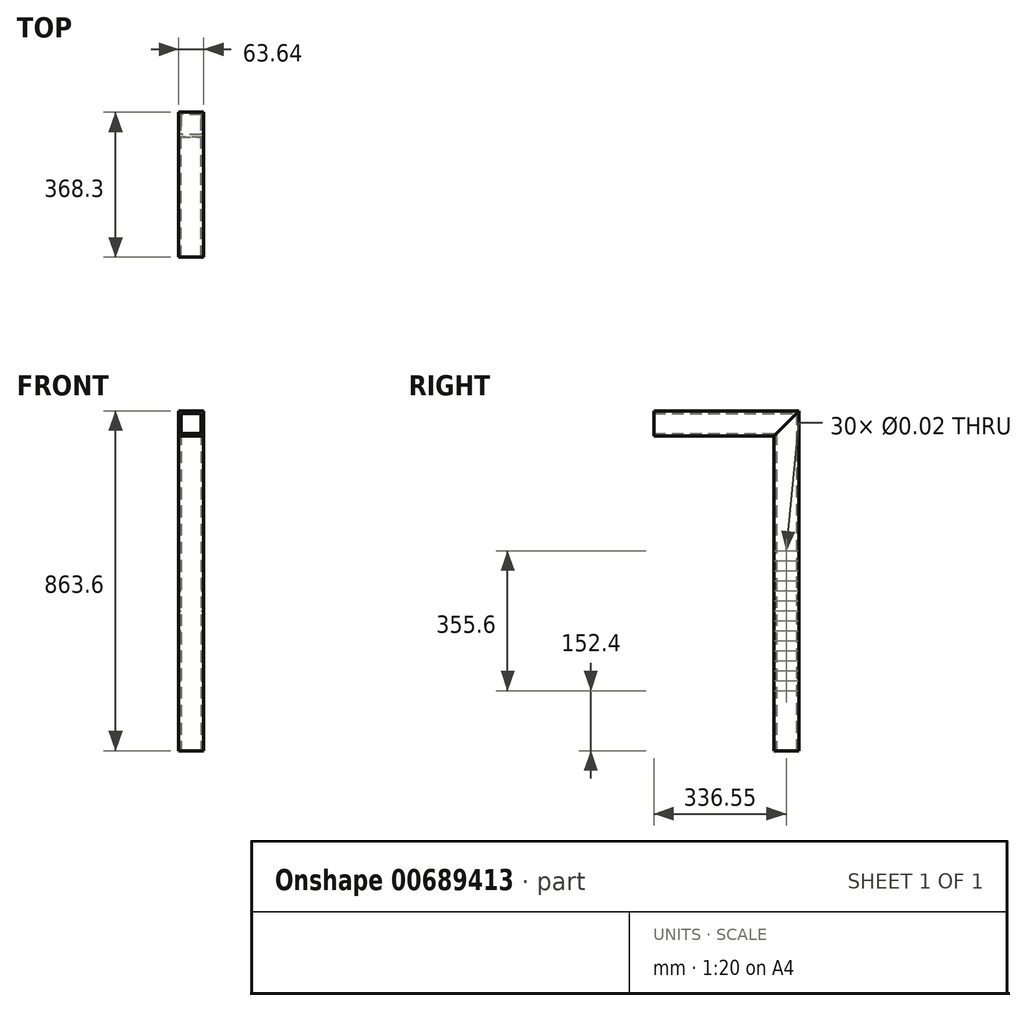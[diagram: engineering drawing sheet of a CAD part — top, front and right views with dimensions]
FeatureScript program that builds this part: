
annotation { "Feature Type Name" : "Feature", "Feature Type Description" : "" }
export const myFeature = defineFeature(function(context is Context, id is Id, definition is map)
    precondition{}
    {
        {
            var Q0;
            Q0=qCreatedBy(makeId("Top.planeOp"),FACE);
            var sketch = newSketch(context, id + "F0", { "sketchPlane" : qUnion([Q0])});
            skLineSegment(sketch, "E0.bottom", {"start": v(-31.75, 31.75) * mm, "end": v(31.75, 31.75) * mm});
            skLineSegment(sketch, "E0.top", {"start": v(-31.75, -31.75) * mm, "end": v(31.75, -31.75) * mm});
            skLineSegment(sketch, "E0.left", {"start": v(-31.75, 31.75) * mm, "end": v(-31.75, -31.75) * mm});
            skLineSegment(sketch, "E0.right", {"start": v(31.75, 31.75) * mm, "end": v(31.75, -31.75) * mm});
            skPoint(sketch, "E0.middle", {"position": v(0, 0) * mm});
            skLineSegment(sketch, "E1.bottom", {"start": v(-25.4, 25.4) * mm, "end": v(25.4, 25.4) * mm});
            skLineSegment(sketch, "E1.top", {"start": v(-25.4, -25.4) * mm, "end": v(25.4, -25.4) * mm});
            skLineSegment(sketch, "E1.left", {"start": v(-25.4, 25.4) * mm, "end": v(-25.4, -25.4) * mm});
            skLineSegment(sketch, "E1.right", {"start": v(25.4, 25.4) * mm, "end": v(25.4, -25.4) * mm});
            skSolve(sketch);
        }
        {
            var Q0;
            Q0=makeQuery(id+"F0.imprint","IMPRINT",FACE,{"disambiguationData":[TD([[makeQuery(id+"F0.imprint","IMPRINT",EDGE,{"derivedFrom":sQuery(id+"F0.wireOp",EDGE,"E0.bottom")}),-1.0]])]});
            extrude(context, id + "F1", {"entities" : qUnion([Q0]), "depth" : 863.6 * mm, "offsetDistance" : 25.4 * mm});
        }
        {
            var Q0;
            Q0=makeQuery(id+"F1.opExtrude","SWEPT_FACE",FACE,{"disambiguationData":[OSD([sQuery(id+"F0.wireOp",EDGE,"E0.right")])]});
            var sketch = newSketch(context, id + "F2", { "sketchPlane" : qUnion([Q0])});
            skLineSegment(sketch, "E2", {"start": v(31.75, 863.6) * mm, "end": v(-31.75, 863.6) * mm});
            skLineSegment(sketch, "E3", {"start": v(-31.75, 863.6) * mm, "end": v(-31.75, 800.1) * mm});
            skLineSegment(sketch, "E4", {"start": v(-31.75, 800.1) * mm, "end": v(31.75, 863.6) * mm});
            skSolve(sketch);
        }
        {
            var Q0;
            Q0=makeQuery(id+"F2.imprint","IMPRINT",FACE,{"disambiguationData":[TD([[makeQuery(id+"F2.imprint","IMPRINT",EDGE,{"derivedFrom":sQuery(id+"F2.wireOp",EDGE,"E2")}),1.0]])]});
            extrude(context, id + "F3", {"entities" : qUnion([Q0]), "operationType" : NewBodyOperationType.REMOVE, "oppositeDirection" : true, "depth" : 63.5 * mm, "offsetDistance" : 25.4 * mm});
        }
        {
            var Q0;
            Q0=makeQuery(id+"F1.opExtrude","SWEPT_FACE",FACE,{"disambiguationData":[OSD([sQuery(id+"F0.wireOp",EDGE,"E0.right")])]});
            var sketch = newSketch(context, id + "F4", { "sketchPlane" : qUnion([Q0])});
            skPoint(sketch, "E5", {"position": v(0, 152.4) * mm});
            skPoint(sketch, "E6.0.1.0", {"position": v(0, 177.8) * mm});
            skPoint(sketch, "E6.0.2.0", {"position": v(0, 203.2) * mm});
            skPoint(sketch, "E6.0.3.0", {"position": v(0, 228.6) * mm});
            skPoint(sketch, "E6.0.4.0", {"position": v(0, 254) * mm});
            skPoint(sketch, "E6.0.5.0", {"position": v(0, 279.4) * mm});
            skPoint(sketch, "E6.0.6.0", {"position": v(0, 304.8) * mm});
            skPoint(sketch, "E6.0.7.0", {"position": v(0, 330.2) * mm});
            skPoint(sketch, "E6.0.8.0", {"position": v(0, 355.6) * mm});
            skPoint(sketch, "E6.0.9.0", {"position": v(0, 381) * mm});
            skPoint(sketch, "E6.0.10.0", {"position": v(0, 406.4) * mm});
            skPoint(sketch, "E6.0.11.0", {"position": v(0, 431.8) * mm});
            skPoint(sketch, "E6.0.12.0", {"position": v(0, 457.2) * mm});
            skPoint(sketch, "E6.0.13.0", {"position": v(0, 482.6) * mm});
            skPoint(sketch, "E6.0.14.0", {"position": v(0, 508) * mm});
            skLineSegment(sketch, "E6.direction1", {"start": v(0, 152.4) * mm, "end": v(25.4, 152.4) * mm, "construction": true});
            skLineSegment(sketch, "E6.direction2", {"start": v(0, 152.4) * mm, "end": v(0, 177.8) * mm, "construction": true});
            skSolve(sketch);
        }
        {
            var Q0;
            Q0=sQuery(id+"F4.wireOp",VERTEX,"E5");
            var Q1;
            Q1=sQuery(id+"F4.wireOp",VERTEX,"E6.0.1.0");
            var Q2;
            Q2=sQuery(id+"F4.wireOp",VERTEX,"E6.0.2.0");
            var Q3;
            Q3=sQuery(id+"F4.wireOp",VERTEX,"E6.0.3.0");
            var Q4;
            Q4=sQuery(id+"F4.wireOp",VERTEX,"E6.0.4.0");
            var Q5;
            Q5=sQuery(id+"F4.wireOp",VERTEX,"E6.0.5.0");
            var Q6;
            Q6=sQuery(id+"F4.wireOp",VERTEX,"E6.0.6.0");
            var Q7;
            Q7=sQuery(id+"F4.wireOp",VERTEX,"E6.0.7.0");
            var Q8;
            Q8=sQuery(id+"F4.wireOp",VERTEX,"E6.0.8.0");
            var Q9;
            Q9=sQuery(id+"F4.wireOp",VERTEX,"E6.0.9.0");
            var Q10;
            Q10=sQuery(id+"F4.wireOp",VERTEX,"E6.0.11.0");
            var Q11;
            Q11=sQuery(id+"F4.wireOp",VERTEX,"E6.0.10.0");
            var Q12;
            Q12=sQuery(id+"F4.wireOp",VERTEX,"E6.0.12.0");
            var Q13;
            Q13=sQuery(id+"F4.wireOp",VERTEX,"E6.0.13.0");
            var Q14;
            Q14=sQuery(id+"F4.wireOp",VERTEX,"E6.0.14.0");
            var Q15;
            Q15=makeQuery(id+"F1.opExtrude","SWEPT_BODY",BODY,{"disambiguationData":[OSD([sQuery(id+"F0.wireOp",EDGE,"E0.bottom"),sQuery(id+"F0.wireOp",EDGE,"E0.top"),sQuery(id+"F0.wireOp",EDGE,"E0.left"),sQuery(id+"F0.wireOp",EDGE,"E0.right"),sQuery(id+"F0.wireOp",EDGE,"E1.bottom"),sQuery(id+"F0.wireOp",EDGE,"E1.top"),sQuery(id+"F0.wireOp",EDGE,"E1.left"),sQuery(id+"F0.wireOp",EDGE,"E1.right")])]});
            hole(context, id + "F5", {"style" : HoleStyle.SIMPLE, "endStyle" : HoleEndStyle.THROUGH, "standardTappedOrClearance" : lookupTablePath({ "standard" : "ANSI", "size" : "1/2 (0.5)", "type" : "Drilled" }), "standardBlindInLast" : lookupTablePath({ "standard" : "ANSI", "size" : "1/2", "type" : "Drilled" }), "holeDiameter" : 1 / 50.8 * mm, "majorDiameter" : 6.35 * mm, "tappedDepth" : 10.3 * mm, "tapClearance" : 3, "locations" : qUnion([Q0, Q1, Q2, Q3, Q4, Q5, Q6, Q7, Q8, Q9, Q10, Q11, Q12, Q13, Q14]), "scope" : qUnion([Q15])});
        }
        {
            var Q0;
            Q0=qCreatedBy(makeId("Front.planeOp"),FACE);
            var sketch = newSketch(context, id + "F6", { "sketchPlane" : qUnion([Q0])});
            skLineSegment(sketch, "E7.bottom", {"start": v(31.6, 0) * mm, "end": v(-31.9, 0) * mm});
            skLineSegment(sketch, "E7.top", {"start": v(31.6, -63.5) * mm, "end": v(-31.9, -63.5) * mm});
            skLineSegment(sketch, "E7.left", {"start": v(31.6, 0) * mm, "end": v(31.6, -63.5) * mm});
            skLineSegment(sketch, "E7.right", {"start": v(-31.9, 0) * mm, "end": v(-31.9, -63.5) * mm});
            skLineSegment(sketch, "E8.bottom", {"start": v(25.4, -6.35) * mm, "end": v(-25.4, -6.35) * mm});
            skLineSegment(sketch, "E8.top", {"start": v(25.4, -57.15) * mm, "end": v(-25.4, -57.15) * mm});
            skLineSegment(sketch, "E8.left", {"start": v(25.4, -6.35) * mm, "end": v(25.4, -57.15) * mm});
            skLineSegment(sketch, "E8.right", {"start": v(-25.4, -6.35) * mm, "end": v(-25.4, -57.15) * mm});
            skPoint(sketch, "E8.middle", {"position": v(0, -31.75) * mm});
            skSolve(sketch);
        }
        {
            var Q0;
            Q0=makeQuery(id+"F6.imprint","IMPRINT",FACE,{"disambiguationData":[TD([[makeQuery(id+"F6.imprint","IMPRINT",EDGE,{"derivedFrom":sQuery(id+"F6.wireOp",EDGE,"E7.bottom")}),1.0]])]});
            extrude(context, id + "F7", {"entities" : qUnion([Q0]), "depth" : 368.3 * mm, "offsetDistance" : 25.4 * mm});
        }
        {
            var Q0;
            Q0=makeQuery(id+"F7.opExtrude","SWEPT_BODY",BODY,{"disambiguationData":[OSD([sQuery(id+"F6.wireOp",EDGE,"E7.bottom"),sQuery(id+"F6.wireOp",EDGE,"E7.top"),sQuery(id+"F6.wireOp",EDGE,"E7.left"),sQuery(id+"F6.wireOp",EDGE,"E7.right"),sQuery(id+"F6.wireOp",EDGE,"E8.bottom"),sQuery(id+"F6.wireOp",EDGE,"E8.top"),sQuery(id+"F6.wireOp",EDGE,"E8.left"),sQuery(id+"F6.wireOp",EDGE,"E8.right")])]});
            var Q1;
            Q1=qCreatedBy(makeId("Front.planeOp"),FACE);
            transform(context, id + "F8", {"entities" : qUnion([Q0]), "transformType" : TransformType.TRANSLATION_DISTANCE, "transformDirection" : qUnion([Q1]), "distance" : 31.75 * mm, "oppositeDirection" : true, "makeCopy" : false});
        }
        {
            var Q0;
            Q0=makeQuery(id+"F7.opExtrude","SWEPT_FACE",FACE,{"disambiguationData":[OSD([sQuery(id+"F6.wireOp",EDGE,"E7.right")])]});
            var sketch = newSketch(context, id + "F9", { "sketchPlane" : qUnion([Q0])});
            skLineSegment(sketch, "E9", {"start": v(-31.75, 0) * mm, "end": v(-31.75, -63.5) * mm});
            skLineSegment(sketch, "E10", {"start": v(-31.75, -63.5) * mm, "end": v(31.75, -63.5) * mm});
            skLineSegment(sketch, "E11", {"start": v(31.75, -63.5) * mm, "end": v(-31.75, 0) * mm});
            skSolve(sketch);
        }
        {
            var Q0;
            Q0=makeQuery(id+"F9.imprint","IMPRINT",FACE,{"disambiguationData":[TD([[makeQuery(id+"F9.imprint","IMPRINT",EDGE,{"derivedFrom":sQuery(id+"F9.wireOp",EDGE,"E9")}),1.0]])]});
            extrude(context, id + "F10", {"entities" : qUnion([Q0]), "operationType" : NewBodyOperationType.REMOVE, "oppositeDirection" : true, "depth" : 63.5 * mm, "offsetDistance" : 25.4 * mm});
        }
        {
            var Q0;
            Q0=makeQuery(id+"F7.opExtrude","SWEPT_BODY",BODY,{"disambiguationData":[OSD([sQuery(id+"F6.wireOp",EDGE,"E7.bottom"),sQuery(id+"F6.wireOp",EDGE,"E7.top"),sQuery(id+"F6.wireOp",EDGE,"E7.left"),sQuery(id+"F6.wireOp",EDGE,"E7.right"),sQuery(id+"F6.wireOp",EDGE,"E8.bottom"),sQuery(id+"F6.wireOp",EDGE,"E8.top"),sQuery(id+"F6.wireOp",EDGE,"E8.left"),sQuery(id+"F6.wireOp",EDGE,"E8.right")])]});
            var Q1;
            Q1=qCreatedBy(makeId("Top.planeOp"),FACE);
            transform(context, id + "F11", {"entities" : qUnion([Q0]), "transformType" : TransformType.TRANSLATION_DISTANCE, "transformDirection" : qUnion([Q1]), "distance" : 863.6 * mm, "makeCopy" : false});
        }
    });
